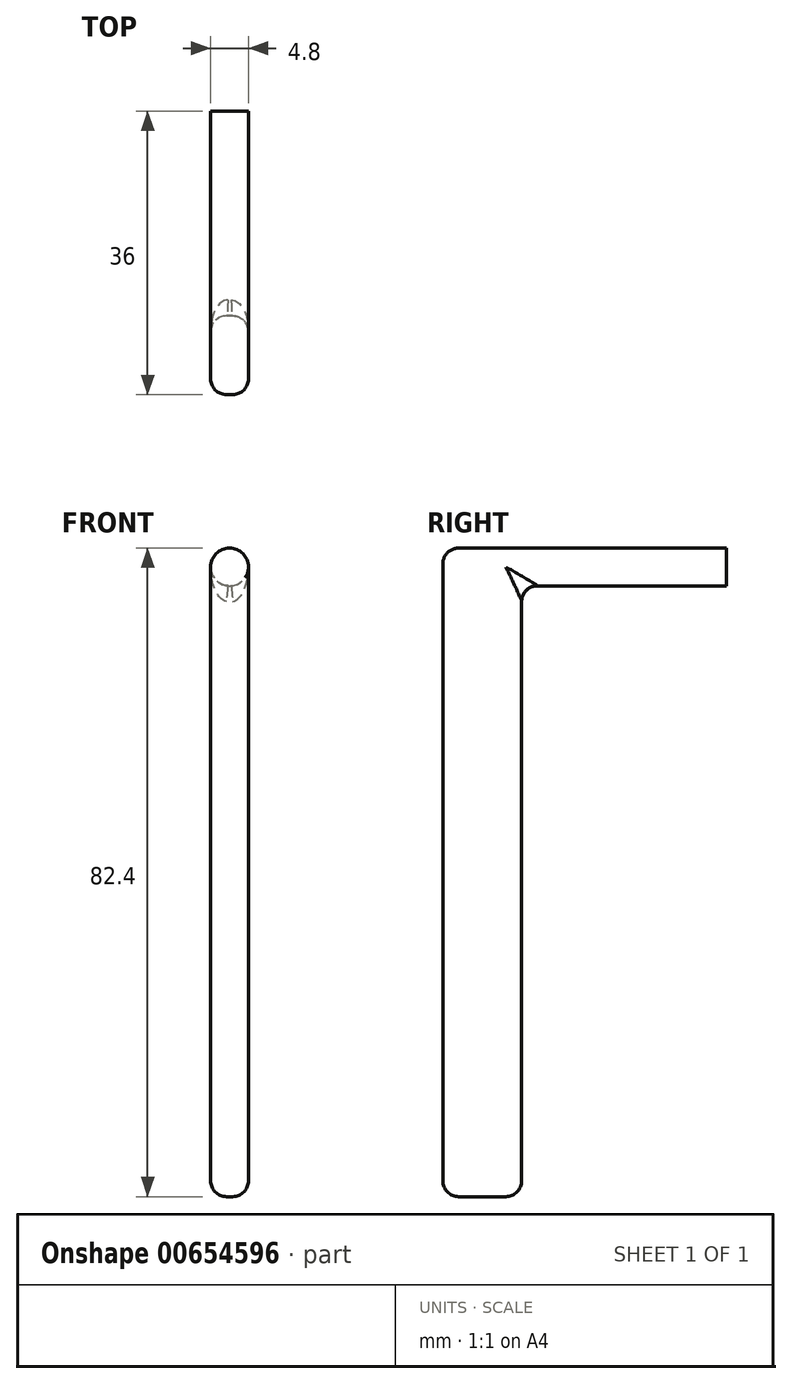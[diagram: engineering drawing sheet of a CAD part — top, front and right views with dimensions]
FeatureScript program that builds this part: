
annotation { "Feature Type Name" : "Feature", "Feature Type Description" : "" }
export const myFeature = defineFeature(function(context is Context, id is Id, definition is map)
    precondition{}
    {
        {
            var Q0;
            Q0=qCreatedBy(makeId("Front.planeOp"),FACE);
            var sketch = newSketch(context, id + "F0", { "sketchPlane" : qUnion([Q0])});
            skCircle(sketch, "E0", {"center": v(0, 0) * mm, "radius": 2.4 * mm});
            skSolve(sketch);
        }
        {
            var Q0;
            Q0=makeQuery(id+"F0.imprint","IMPRINT",FACE,{"disambiguationData":[TD([[makeQuery(id+"F0.imprint","IMPRINT",EDGE,{"derivedFrom":sQuery(id+"F0.wireOp",EDGE,"E0")}),1.0]])]});
            extrude(context, id + "F1", {"entities" : qUnion([Q0]), "depth" : 26 * mm, "offsetDistance" : 25 * mm});
        }
        {
            var Q0;
            Q0=makeQuery(id+"F1.opExtrude","CAP_FACE",FACE,{"disambiguationData":[OSD([sQuery(id+"F0.wireOp",EDGE,"E0")])],"isStart":false});
            var sketch = newSketch(context, id + "F2", { "sketchPlane" : qUnion([Q0])});
            skArc(sketch, "E1", {"start": v(2.4, 0) * mm, "mid": v(0, 2.4) * mm, "end": v(-2.4, 0) * mm});
            skLineSegment(sketch, "E2", {"start": v(-2.4, 0) * mm, "end": v(-2.4, -80) * mm});
            skLineSegment(sketch, "E3", {"start": v(2.4, 0) * mm, "end": v(2.4, -80) * mm});
            skLineSegment(sketch, "E4", {"start": v(2.4, -80) * mm, "end": v(-2.4, -80) * mm});
            skSolve(sketch);
        }
        {
            var Q0;
            Q0 = qSketchRegion(id + "F2", true);
            extrude(context, id + "F3", {"entities" : qUnion([Q0]), "operationType" : NewBodyOperationType.ADD, "depth" : 10 * mm, "offsetDistance" : 25 * mm});
        }
        {
            var Q0;
            Q0=makeQuery(id+"F3.opExtrude","CAP_FACE",FACE,{"disambiguationData":[OSD([sQuery(id+"F2.wireOp",EDGE,"E1"),sQuery(id+"F2.wireOp",EDGE,"E2"),sQuery(id+"F2.wireOp",EDGE,"E3"),sQuery(id+"F2.wireOp",EDGE,"E4")])],"isStart":false});
            var Q1;
            Q1=makeQuery(id+"F3.opExtrude","SWEPT_FACE",FACE,{"disambiguationData":[OSD([sQuery(id+"F2.wireOp",EDGE,"E2")])]});
            var Q2;
            Q2=makeQuery(id+"F3.opExtrude","SWEPT_FACE",FACE,{"disambiguationData":[OSD([sQuery(id+"F2.wireOp",EDGE,"E4")])]});
            var Q3;
            Q3=makeQuery(id+"F3.opExtrude","SWEPT_FACE",FACE,{"disambiguationData":[OSD([sQuery(id+"F2.wireOp",EDGE,"E3")])]});
            var Q4;
            Q4=makeQuery(id+"F3.opExtrude","CAP_FACE",FACE,{"disambiguationData":[OSD([sQuery(id+"F2.wireOp",EDGE,"E1"),sQuery(id+"F2.wireOp",EDGE,"E2"),sQuery(id+"F2.wireOp",EDGE,"E3"),sQuery(id+"F2.wireOp",EDGE,"E4")])],"isStart":true});
            fillet(context, id + "F4", {"entities" : qUnion([Q0, Q1, Q2, Q3, Q4]), "radius" : 2 * mm, "tangentPropagation" : true, "allowEdgeOverflow" : false});
        }
    });
